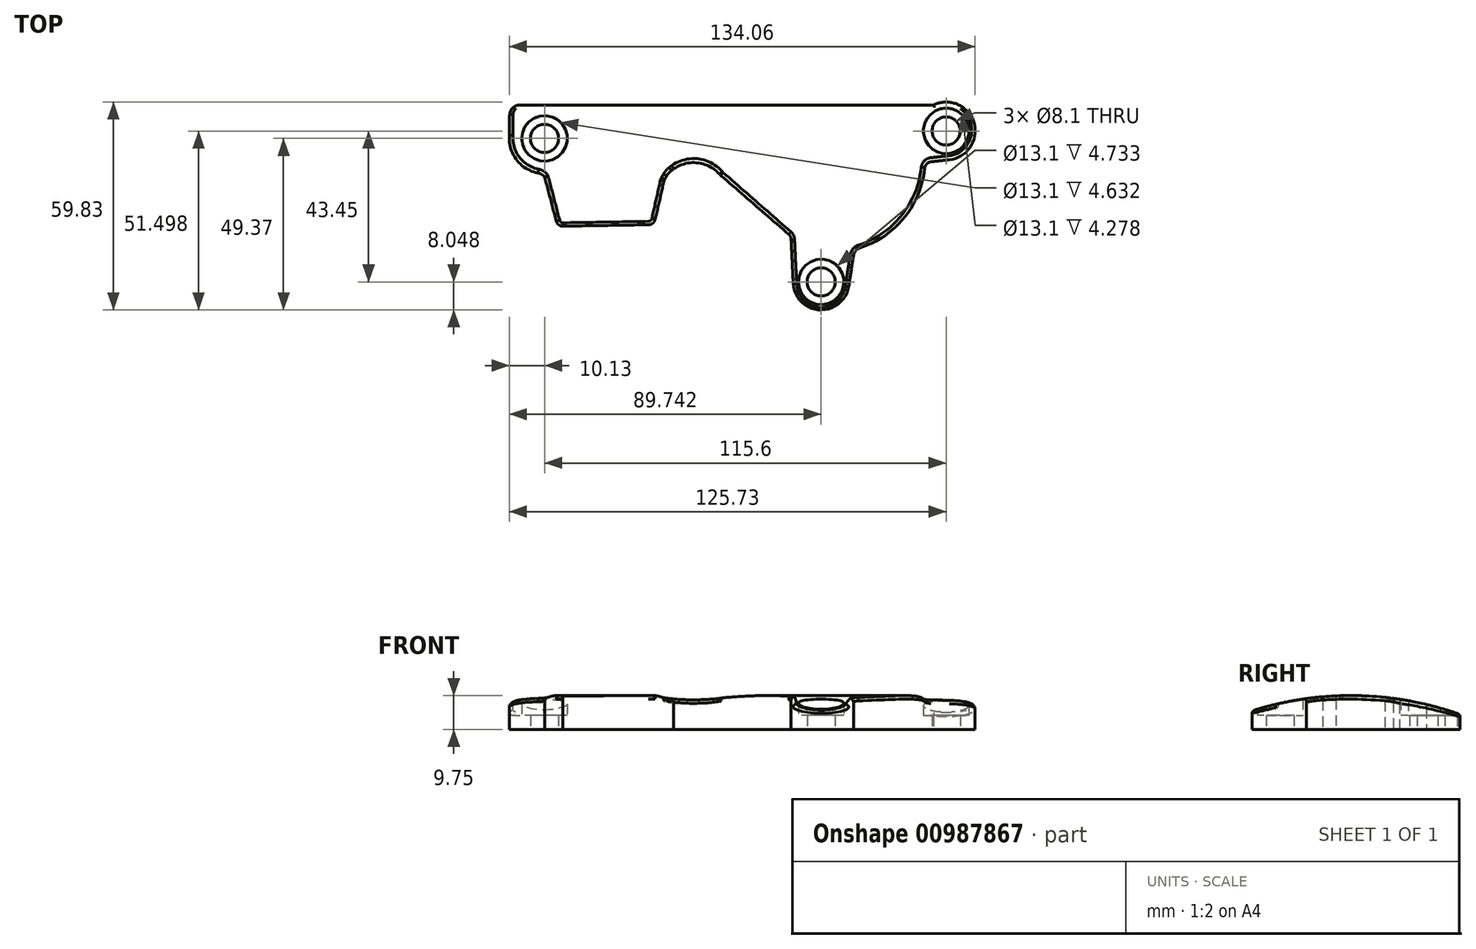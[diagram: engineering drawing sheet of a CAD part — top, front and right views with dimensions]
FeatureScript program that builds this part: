
annotation { "Feature Type Name" : "Feature", "Feature Type Description" : "" }
export const myFeature = defineFeature(function(context is Context, id is Id, definition is map)
    precondition{}
    {
        {
            var Q0;
            Q0=qCreatedBy(makeId("Top.planeOp"),FACE);
            var sketch = newSketch(context, id + "F0", { "sketchPlane" : qUnion([Q0])});
            skLineSegment(sketch, "E0.bottom", {"start": v(-41.75, 1.1) * mm, "end": v(-47.05, 1.1) * mm});
            skLineSegment(sketch, "E0.top", {"start": v(-11.03, 60.1) * mm, "end": v(-125, 60.1) * mm});
            skCircle(sketch, "E1", {"center": v(-7.4, 52.6) * mm, "radius": 4.05 * mm});
            skPoint(sketch, "E2.visualSharp", {"position": v(1.65, 60.1) * mm});
            skCircle(sketch, "E3", {"center": v(-123, 50.48) * mm, "radius": 4.05 * mm});
            skPoint(sketch, "E4.visualSharp", {"position": v(-133, 60.1) * mm});
            skCircle(sketch, "E5", {"center": v(-43.39, 9.16) * mm, "radius": 4.05 * mm});
            skLineSegment(sketch, "E6", {"start": v(-7.4, 43.56) * mm, "end": v(-7.4, 43.56) * mm});
            skCircle(sketch, "E7", {"center": v(-7.4, 52.6) * mm, "radius": 6.55 * mm});
            skCircle(sketch, "E8", {"center": v(-123, 50.48) * mm, "radius": 6.55 * mm});
            skCircle(sketch, "E9", {"center": v(-43.39, 9.16) * mm, "radius": 6.55 * mm});
            skPoint(sketch, "E10.visualSharp", {"position": v(-19.8, 43.56) * mm});
            skArc(sketch, "E11", {"start": v(-133.1, 51.26) * mm, "mid": v(-131.03, 44.3) * mm, "end": v(-124.85, 40.52) * mm});
            skLineSegment(sketch, "E12", {"start": v(-123.6, 44.12) * mm, "end": v(-123.6, 43.96) * mm});
            skPoint(sketch, "E13.visualSharp", {"position": v(-123.7, 40.37) * mm});
            skArc(sketch, "E13.filletArc", {"start": v(-122.93, 39.28) * mm, "mid": v(-123.77, 40.09) * mm, "end": v(-124.85, 40.52) * mm});
            skLineSegment(sketch, "E14", {"start": v(-72.24, 39.78) * mm, "end": v(-52.73, 22.88) * mm});
            skArc(sketch, "E15", {"start": v(-72.67, 40.2) * mm, "mid": v(-78.96, 43.43) * mm, "end": v(-85.81, 41.7) * mm});
            skArc(sketch, "E16.filletArc", {"start": v(-32.71, 18.8) * mm, "mid": v(-33.63, 17.92) * mm, "end": v(-34.1, 16.74) * mm});
            skPoint(sketch, "E17.second.point", {"position": v(-31.6, 19.36) * mm});
            skPoint(sketch, "E17.third.point", {"position": v(-65.98, 65.16) * mm});
            skPoint(sketch, "E18.visualSharp", {"position": v(-16.19, 43.56) * mm});
            skPoint(sketch, "E19.visualSharp", {"position": v(-117.53, 23.5) * mm});
            skLineSegment(sketch, "E20.bottom", {"start": v(-108.25, 53.1) * mm, "end": v(-96.88, 53.1) * mm});
            skLineSegment(sketch, "E20.top", {"start": v(-108.25, 34.1) * mm, "end": v(-96.88, 34.1) * mm});
            skLineSegment(sketch, "E20.left", {"start": v(-110.25, 51.1) * mm, "end": v(-110.25, 36.1) * mm});
            skLineSegment(sketch, "E20.right", {"start": v(-94.88, 51.1) * mm, "end": v(-94.88, 36.1) * mm});
            skPoint(sketch, "E21.visualSharp", {"position": v(-110.25, 53.1) * mm});
            skArc(sketch, "E21.filletArc", {"start": v(-108.25, 53.1) * mm, "mid": v(-109.66, 52.52) * mm, "end": v(-110.25, 51.1) * mm});
            skPoint(sketch, "E22.visualSharp", {"position": v(-94.88, 53.1) * mm});
            skArc(sketch, "E22.filletArc", {"start": v(-94.88, 51.1) * mm, "mid": v(-95.47, 52.52) * mm, "end": v(-96.88, 53.1) * mm});
            skPoint(sketch, "E23.visualSharp", {"position": v(-94.88, 34.1) * mm});
            skArc(sketch, "E23.filletArc", {"start": v(-96.88, 34.1) * mm, "mid": v(-95.47, 34.7) * mm, "end": v(-94.88, 36.1) * mm});
            skPoint(sketch, "E24.visualSharp", {"position": v(-110.25, 34.1) * mm});
            skArc(sketch, "E24.filletArc", {"start": v(-110.25, 36.1) * mm, "mid": v(-109.66, 34.7) * mm, "end": v(-108.25, 34.1) * mm});
            skLineSegment(sketch, "E25", {"start": v(-57.85, 43.36) * mm, "end": v(-36.96, 43.36) * mm, "construction": true});
            skLineSegment(sketch, "E26", {"start": v(-38.9, 66.84) * mm, "end": v(-38.9, 34.41) * mm, "construction": true});
            skLineSegment(sketch, "E27", {"start": v(-83.71, 52.28) * mm, "end": v(-59.8, 52.28) * mm, "construction": true});
            skArc(sketch, "E28", {"start": v(-6.49, 44.33) * mm, "mid": v(0.6, 54.91) * mm, "end": v(-11.03, 60.1) * mm});
            skLineSegment(sketch, "E29", {"start": v(-11.8, 43.74) * mm, "end": v(-6.49, 44.33) * mm});
            skLineSegment(sketch, "E30", {"start": v(-122.93, 39.28) * mm, "end": v(-119.62, 26.7) * mm});
            skPoint(sketch, "E31.visualSharp", {"position": v(-119.23, 25.2) * mm});
            skArc(sketch, "E31.filletArc", {"start": v(-119.62, 26.7) * mm, "mid": v(-118.91, 25.62) * mm, "end": v(-117.7, 25.2) * mm});
            skPoint(sketch, "E32.visualSharp", {"position": v(-52.02, 22.27) * mm});
            skArc(sketch, "E32.filletArc", {"start": v(-52.04, 21.37) * mm, "mid": v(-52.22, 22.2) * mm, "end": v(-52.73, 22.88) * mm});
            skArc(sketch, "E33", {"start": v(-51.43, 8.77) * mm, "mid": v(-43.8, 1.12) * mm, "end": v(-35.43, 7.96) * mm});
            skLineSegment(sketch, "E34", {"start": v(-52.04, 21.37) * mm, "end": v(-51.43, 8.77) * mm});
            skLineSegment(sketch, "E35", {"start": v(-34.1, 16.74) * mm, "end": v(-35.43, 7.96) * mm});
            skLineSegment(sketch, "E36", {"start": v(-38.39, 28.06) * mm, "end": v(-38.39, -13.65) * mm, "construction": true});
            skArc(sketch, "E37", {"start": v(-32.7, 18.8) * mm, "mid": v(-19.62, 27.48) * mm, "end": v(-13.57, 41.96) * mm});
            skPoint(sketch, "E38.visualSharp", {"position": v(-32.7, 18.8) * mm});
            skArc(sketch, "E38.filletArc", {"start": v(-32.7, 18.8) * mm, "mid": v(-32.7, 18.8) * mm, "end": v(-32.71, 18.8) * mm});
            skPoint(sketch, "E39.visualSharp", {"position": v(-13.46, 43.56) * mm});
            skArc(sketch, "E39.filletArc", {"start": v(-13.39, 43.57) * mm, "mid": v(-13.44, 43.54) * mm, "end": v(-13.46, 43.49) * mm});
            skArc(sketch, "E40.filletArc", {"start": v(-11.8, 43.74) * mm, "mid": v(-13, 43.16) * mm, "end": v(-13.57, 41.96) * mm});
            skLineSegment(sketch, "E41", {"start": v(-125, 60.1) * mm, "end": v(-130.03, 60.1) * mm});
            skLineSegment(sketch, "E42", {"start": v(-133.1, 51.26) * mm, "end": v(-133.03, 57.14) * mm});
            skArc(sketch, "E43.filletArc", {"start": v(-130.03, 60.1) * mm, "mid": v(-132.14, 59.24) * mm, "end": v(-133.03, 57.14) * mm});
            skPoint(sketch, "E44.visualSharp", {"position": v(-85.54, 41.88) * mm});
            skPoint(sketch, "E45.visualSharp", {"position": v(-87, 39.7) * mm});
            skLineSegment(sketch, "E46", {"start": v(-88.65, 38.1) * mm, "end": v(-91.14, 27.18) * mm});
            skLineSegment(sketch, "E47", {"start": v(-117.7, 25.2) * mm, "end": v(-93.06, 25.62) * mm});
            skLineSegment(sketch, "E48", {"start": v(-88.44, 38.65) * mm, "end": v(-87.87, 39.64) * mm});
            skPoint(sketch, "E48.endSnap0", {"position": v(-87.35, 39.97) * mm});
            skLineSegment(sketch, "E49", {"start": v(-86.5, 41.19) * mm, "end": v(-85.81, 41.7) * mm});
            skPoint(sketch, "E44.filletArc.end.orphan", {"position": v(-87, 40.56) * mm});
            skPoint(sketch, "E45.filletArc.end.orphan", {"position": v(-88.06, 38.4) * mm});
            skPoint(sketch, "E45.filletArc.start.orphan", {"position": v(-87.7, 39.38) * mm});
            skPoint(sketch, "E50.visualSharp", {"position": v(-91.5, 25.65) * mm});
            skArc(sketch, "E50.filletArc", {"start": v(-93.06, 25.62) * mm, "mid": v(-91.83, 26.07) * mm, "end": v(-91.14, 27.18) * mm});
            skPoint(sketch, "E51.visualSharp", {"position": v(-88.58, 38.4) * mm});
            skArc(sketch, "E51.filletArc", {"start": v(-88.44, 38.65) * mm, "mid": v(-88.56, 38.38) * mm, "end": v(-88.65, 38.1) * mm});
            skPoint(sketch, "E52.visualSharp", {"position": v(-87.35, 40.56) * mm});
            skArc(sketch, "E52.filletArc", {"start": v(-86.5, 41.19) * mm, "mid": v(-87.27, 40.49) * mm, "end": v(-87.87, 39.64) * mm});
            skCircle(sketch, "E53", {"center": v(-37.4, 40.86) * mm, "radius": 7 * mm});
            skPoint(sketch, "E54.visualSharp", {"position": v(-72.49, 40) * mm});
            skArc(sketch, "E54.filletArc", {"start": v(-72.67, 40.2) * mm, "mid": v(-72.46, 39.99) * mm, "end": v(-72.24, 39.78) * mm});
            skSolve(sketch);
        }
        {
            var Q0;
            Q0=makeQuery(id+"F0.imprint","IMPRINT",FACE,{"disambiguationData":[TD([[makeQuery(id+"F0.imprint","IMPRINT",EDGE,{"derivedFrom":sQuery(id+"F0.wireOp",EDGE,"KT7OFKYp-8AOP-qHuq-5Vdi-wzPE5hdiJrYk")}),1.0]])]});
            var Q1;
            {var subQ0=sQuery(id+"F0.wireOp",EDGE,"E0.bottom");Q1=makeQuery(id+"F0.imprint","IMPRINT",FACE,{"disambiguationData":[TD([[makeQuery(id+"F0.imprint","IMPRINT",EDGE,{"derivedFrom":subQ0}),-1.0]])]});}
            var Q2;
            Q2=makeQuery(id+"F0.imprint","IMPRINT",FACE,{"disambiguationData":[TD([[makeQuery(id+"F0.imprint","IMPRINT",EDGE,{"derivedFrom":sQuery(id+"F0.wireOp",EDGE,"E1")}),-1.0]])]});
            var Q3;
            Q3=makeQuery(id+"F0.imprint","IMPRINT",FACE,{"disambiguationData":[TD([[makeQuery(id+"F0.imprint","IMPRINT",EDGE,{"derivedFrom":sQuery(id+"F0.wireOp",EDGE,"E5")}),-1.0]])]});
            var Q4;
            Q4=makeQuery(id+"F0.imprint","IMPRINT",FACE,{"disambiguationData":[TD([[makeQuery(id+"F0.imprint","IMPRINT",EDGE,{"derivedFrom":sQuery(id+"F0.wireOp",EDGE,"6RRhr83a-xgTF-1fLh-GwAI-x98koxkOzZaD.bottom")}),-1.0]])]});
            var Q5;
            {var subQ10=sQuery(id+"F0.wireOp",EDGE,"E0.top");Q5=makeQuery(id+"F0.imprint","IMPRINT",FACE,{"disambiguationData":[TD([[makeQuery(id+"F0.imprint","IMPRINT",EDGE,{"derivedFrom":subQ10}),1.0]])]});}
            var Q6;
            Q6=makeQuery(id+"F0.imprint","IMPRINT",FACE,{"disambiguationData":[TD([[makeQuery(id+"F0.imprint","IMPRINT",EDGE,{"derivedFrom":sQuery(id+"F0.wireOp",EDGE,"E3")}),-1.0]])]});
            var Q7;
            Q7=makeQuery(id+"F0.imprint","IMPRINT",FACE,{"disambiguationData":[TD([[makeQuery(id+"F0.imprint","IMPRINT",EDGE,{"derivedFrom":sQuery(id+"F0.wireOp",EDGE,"E20.bottom")}),-1.0]])]});
            var Q8;
            Q8=makeQuery(id+"F0.imprint","IMPRINT",FACE,{"disambiguationData":[TD([[makeQuery(id+"F0.imprint","IMPRINT",EDGE,{"derivedFrom":sQuery(id+"F0.wireOp",EDGE,"E53")}),1.0]])]});
            extrude(context, id + "F1", {"entities" : qUnion([Q0, Q1, Q2, Q3, Q4, Q5, Q6, Q7, Q8]), "depth" : 10 * mm, "offsetDistance" : 25 * mm});
        }
        {
            var Q0;
            Q0=makeQuery(id+"F0.imprint","IMPRINT",FACE,{"disambiguationData":[TD([[makeQuery(id+"F0.imprint","IMPRINT",EDGE,{"derivedFrom":sQuery(id+"F0.wireOp",EDGE,"KT7OFKYp-8AOP-qHuq-5Vdi-wzPE5hdiJrYk")}),1.0]])]});
            var Q1;
            Q1=makeQuery(id+"F1.opExtrude","CAP_FACE",FACE,{"disambiguationData":[OSD([sQuery(id+"F0.wireOp",EDGE,"E0.top"),sQuery(id+"F0.wireOp",EDGE,"E1"),sQuery(id+"F0.wireOp",EDGE,"E3"),sQuery(id+"F0.wireOp",EDGE,"E5"),sQuery(id+"F0.wireOp",EDGE,"E11"),sQuery(id+"F0.wireOp",EDGE,"E13.filletArc"),sQuery(id+"F0.wireOp",EDGE,"E14"),sQuery(id+"F0.wireOp",EDGE,"E15"),sQuery(id+"F0.wireOp",EDGE,"E16.filletArc"),sQuery(id+"F0.wireOp",EDGE,"E20.bottom"),sQuery(id+"F0.wireOp",EDGE,"E20.top"),sQuery(id+"F0.wireOp",EDGE,"E20.left"),sQuery(id+"F0.wireOp",EDGE,"E20.right"),sQuery(id+"F0.wireOp",EDGE,"E21.filletArc"),sQuery(id+"F0.wireOp",EDGE,"E22.filletArc"),sQuery(id+"F0.wireOp",EDGE,"E23.filletArc"),sQuery(id+"F0.wireOp",EDGE,"E24.filletArc"),sQuery(id+"F0.wireOp",EDGE,"E28"),sQuery(id+"F0.wireOp",EDGE,"E29"),sQuery(id+"F0.wireOp",EDGE,"E30"),sQuery(id+"F0.wireOp",EDGE,"E31.filletArc"),sQuery(id+"F0.wireOp",EDGE,"E32.filletArc"),sQuery(id+"F0.wireOp",EDGE,"E33"),sQuery(id+"F0.wireOp",EDGE,"E34"),sQuery(id+"F0.wireOp",EDGE,"E35"),sQuery(id+"F0.wireOp",EDGE,"E37"),sQuery(id+"F0.wireOp",EDGE,"E38.filletArc"),sQuery(id+"F0.wireOp",EDGE,"E40.filletArc"),sQuery(id+"F0.wireOp",EDGE,"E41"),sQuery(id+"F0.wireOp",EDGE,"E42"),sQuery(id+"F0.wireOp",EDGE,"E43.filletArc"),sQuery(id+"F0.wireOp",EDGE,"E46"),sQuery(id+"F0.wireOp",EDGE,"E47"),sQuery(id+"F0.wireOp",EDGE,"E48"),sQuery(id+"F0.wireOp",EDGE,"E49"),sQuery(id+"F0.wireOp",EDGE,"E50.filletArc"),sQuery(id+"F0.wireOp",EDGE,"E51.filletArc"),sQuery(id+"F0.wireOp",EDGE,"E52.filletArc"),sQuery(id+"F0.wireOp",EDGE,"E53")])],"isStart":false});
            extrude(context, id + "F2", {"entities" : qUnion([Q0, Q1]), "operationType" : NewBodyOperationType.REMOVE, "depth" : 5 * mm, "offsetDistance" : 25 * mm});
        }
        {
            var Q0;
            Q0=makeQuery(id+"F0.imprint","IMPRINT",FACE,{"disambiguationData":[TD([[makeQuery(id+"F0.imprint","IMPRINT",EDGE,{"derivedFrom":sQuery(id+"F0.wireOp",EDGE,"E1")}),-1.0]])]});
            var Q1;
            Q1=makeQuery(id+"F0.imprint","IMPRINT",FACE,{"disambiguationData":[TD([[makeQuery(id+"F0.imprint","IMPRINT",EDGE,{"derivedFrom":sQuery(id+"F0.wireOp",EDGE,"E3")}),-1.0]])]});
            var Q2;
            Q2=makeQuery(id+"F0.imprint","IMPRINT",FACE,{"disambiguationData":[TD([[makeQuery(id+"F0.imprint","IMPRINT",EDGE,{"derivedFrom":sQuery(id+"F0.wireOp",EDGE,"E5")}),-1.0]])]});
            extrude(context, id + "F3", {"entities" : qUnion([Q0, Q1, Q2]), "operationType" : NewBodyOperationType.REMOVE, "depth" : 10 * mm, "offsetDistance" : 25 * mm, "hasSecondDirection" : true, "secondDirectionOppositeDirection" : false, "secondDirectionDepth" : 4 * mm});
        }
        {
            var Q0;
            Q0=qCreatedBy(makeId("Right.planeOp"),FACE);
            var sketch = newSketch(context, id + "F4", { "sketchPlane" : qUnion([Q0])});
            skLineSegment(sketch, "E55", {"start": v(-18.75, 5) * mm, "end": v(79.13, 5) * mm, "construction": true});
            skLineSegment(sketch, "E56", {"start": v(29.5, 28.3) * mm, "end": v(29.5, -22.36) * mm, "construction": true});
            skArc(sketch, "E57", {"start": v(58.97, 5) * mm, "mid": v(29.48, 9.75) * mm, "end": v(0, 5) * mm});
            skLineSegment(sketch, "E58", {"start": v(0, 5) * mm, "end": v(0, 14.56) * mm});
            skLineSegment(sketch, "E59", {"start": v(0, 14.56) * mm, "end": v(62.9, 14.56) * mm});
            skLineSegment(sketch, "E60", {"start": v(62.9, 14.56) * mm, "end": v(62.9, 5) * mm});
            skLineSegment(sketch, "E61", {"start": v(62.9, 5) * mm, "end": v(58.97, 5) * mm});
            skLineSegment(sketch, "E62", {"start": v(58.97, 5) * mm, "end": v(61.54, 4.15) * mm});
            skLineSegment(sketch, "E63", {"start": v(61.54, 4.15) * mm, "end": v(62.9, 5) * mm});
            skSolve(sketch);
        }
        {
            var Q0;
            Q0=makeQuery(id+"F4.imprint","IMPRINT",FACE,{"disambiguationData":[TD([[makeQuery(id+"F4.imprint","IMPRINT",EDGE,{"derivedFrom":sQuery(id+"F4.wireOp",EDGE,"E57")}),-1.0]])]});
            var Q1;
            Q1=makeQuery(id+"F4.imprint","IMPRINT",FACE,{"disambiguationData":[TD([[makeQuery(id+"F4.imprint","IMPRINT",EDGE,{"derivedFrom":sQuery(id+"F4.wireOp",EDGE,"E61")}),1.0]])]});
            extrude(context, id + "F5", {"entities" : qUnion([Q0, Q1]), "operationType" : NewBodyOperationType.REMOVE, "oppositeDirection" : true, "depth" : 180 * mm, "offsetDistance" : 25 * mm, "hasSecondDirection" : true, "secondDirectionOppositeDirection" : false, "secondDirectionDepth" : 25 * mm});
        }
        {
            var Q0;
            Q0=makeQuery(id+"F5.boolean.opBoolean","INTERSECT",EDGE,{"derivedFrom":[makeQuery(id+"F1.opExtrude","SWEPT_FACE",FACE,{"disambiguationData":[OSD([sQuery(id+"F0.wireOp",EDGE,"E28")])]}),makeQuery(id+"F5.opExtrude","SWEPT_FACE",FACE,{"disambiguationData":[OSD([sQuery(id+"F4.wireOp",EDGE,"E57")])]})]});
            var Q1;
            Q1=makeQuery(id+"F5.boolean.opBoolean","INTERSECT",EDGE,{"derivedFrom":[makeQuery(id+"F1.opExtrude","SWEPT_FACE",FACE,{"disambiguationData":[OSD([sQuery(id+"F0.wireOp",EDGE,"E29")])]}),makeQuery(id+"F5.opExtrude","SWEPT_FACE",FACE,{"disambiguationData":[OSD([sQuery(id+"F4.wireOp",EDGE,"E57")])]})]});
            var Q2;
            Q2=makeQuery(id+"F5.boolean.opBoolean","INTERSECT",EDGE,{"derivedFrom":[makeQuery(id+"F1.opExtrude","SWEPT_FACE",FACE,{"disambiguationData":[OSD([sQuery(id+"F0.wireOp",EDGE,"E40.filletArc")])]}),makeQuery(id+"F5.opExtrude","SWEPT_FACE",FACE,{"disambiguationData":[OSD([sQuery(id+"F4.wireOp",EDGE,"E57")])]})]});
            var Q3;
            Q3=makeQuery(id+"F5.boolean.opBoolean","INTERSECT",EDGE,{"derivedFrom":[makeQuery(id+"F1.opExtrude","SWEPT_FACE",FACE,{"disambiguationData":[OSD([sQuery(id+"F0.wireOp",EDGE,"E37")])]}),makeQuery(id+"F5.opExtrude","SWEPT_FACE",FACE,{"disambiguationData":[OSD([sQuery(id+"F4.wireOp",EDGE,"E57")])]})]});
            var Q4;
            Q4=makeQuery(id+"F5.boolean.opBoolean","INTERSECT",EDGE,{"derivedFrom":[makeQuery(id+"F1.opExtrude","SWEPT_FACE",FACE,{"disambiguationData":[OSD([sQuery(id+"F0.wireOp",EDGE,"E0.top"),sQuery(id+"F0.wireOp",EDGE,"E41")])]}),makeQuery(id+"F5.opExtrude","SWEPT_FACE",FACE,{"disambiguationData":[OSD([sQuery(id+"F4.wireOp",EDGE,"E62")])]})]});
            var Q5;
            Q5=makeQuery(id+"F5.boolean.opBoolean","INTERSECT",EDGE,{"derivedFrom":[makeQuery(id+"F1.opExtrude","SWEPT_FACE",FACE,{"disambiguationData":[OSD([sQuery(id+"F0.wireOp",EDGE,"E35")])]}),makeQuery(id+"F5.opExtrude","SWEPT_FACE",FACE,{"disambiguationData":[OSD([sQuery(id+"F4.wireOp",EDGE,"E57")])]})]});
            var Q6;
            Q6=makeQuery(id+"F5.boolean.opBoolean","INTERSECT",EDGE,{"derivedFrom":[makeQuery(id+"F1.opExtrude","SWEPT_FACE",FACE,{"disambiguationData":[OSD([sQuery(id+"F0.wireOp",EDGE,"E14")])]}),makeQuery(id+"F5.opExtrude","SWEPT_FACE",FACE,{"disambiguationData":[OSD([sQuery(id+"F4.wireOp",EDGE,"E57")])]})]});
            var Q7;
            Q7=makeQuery(id+"F5.boolean.opBoolean","INTERSECT",EDGE,{"derivedFrom":[makeQuery(id+"F1.opExtrude","SWEPT_FACE",FACE,{"disambiguationData":[OSD([sQuery(id+"F0.wireOp",EDGE,"E15")])]}),makeQuery(id+"F5.opExtrude","SWEPT_FACE",FACE,{"disambiguationData":[OSD([sQuery(id+"F4.wireOp",EDGE,"E57")])]})]});
            var Q8;
            Q8=makeQuery(id+"F5.boolean.opBoolean","INTERSECT",EDGE,{"derivedFrom":[makeQuery(id+"F1.opExtrude","SWEPT_FACE",FACE,{"disambiguationData":[OSD([sQuery(id+"F0.wireOp",EDGE,"E46")])]}),makeQuery(id+"F5.opExtrude","SWEPT_FACE",FACE,{"disambiguationData":[OSD([sQuery(id+"F4.wireOp",EDGE,"E57")])]})]});
            var Q9;
            Q9=makeQuery(id+"F5.boolean.opBoolean","INTERSECT",EDGE,{"derivedFrom":[makeQuery(id+"F1.opExtrude","SWEPT_FACE",FACE,{"disambiguationData":[OSD([sQuery(id+"F0.wireOp",EDGE,"E11")])]}),makeQuery(id+"F5.opExtrude","SWEPT_FACE",FACE,{"disambiguationData":[OSD([sQuery(id+"F4.wireOp",EDGE,"E57")])]})]});
            var Q10;
            Q10=makeQuery(id+"F5.boolean.opBoolean","INTERSECT",EDGE,{"derivedFrom":[makeQuery(id+"F1.opExtrude","SWEPT_FACE",FACE,{"disambiguationData":[OSD([sQuery(id+"F0.wireOp",EDGE,"E30")])]}),makeQuery(id+"F5.opExtrude","SWEPT_FACE",FACE,{"disambiguationData":[OSD([sQuery(id+"F4.wireOp",EDGE,"E57")])]})]});
            fillet(context, id + "F6", {"entities" : qUnion([Q0, Q1, Q2, Q3, Q4, Q5, Q6, Q7, Q8, Q9, Q10]), "radius" : 1 * mm, "tangentPropagation" : true, "allowEdgeOverflow" : false});
        }
    });
